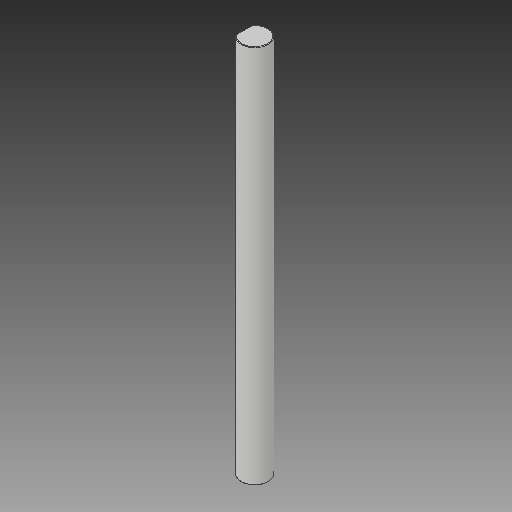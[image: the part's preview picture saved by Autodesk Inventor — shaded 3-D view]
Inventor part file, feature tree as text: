
AUTODESK INVENTOR PART (.ipt)
format: ipt  version: 2019 (Build 230136000, 136)  size: 122,368 bytes
history: native  units: in
note: dims shown in document units (in); Inventor stores cm internally (conversion verified against a paired STEP export)
features: chamfer x1, direct_edit x1, extrude x1, fillet x1, sketch x1, projected_geometry x1, other x1
ambient origin geometry x8: Origin, YZ Plane, XZ Plane, XY Plane, X Axis, Y Axis, Z Axis, Center Point
bodies: Solid1 (feature_tree)
feature tree (7):
  chamfer  "Chamfer1"  Distance=0.505in
  direct_edit  "Direct Edit2"
  extrude  "Extrusion1"  Depth=0.005in
  fillet  "Fillet1"  [1 undecoded]
  sketch  "Sketch1"  dims[d3=-0.005in d4=0.505in d5=0.0in d6=0.005in]
  projected_geometry  "Projected Loop1"
  other  "Size1"
note: 1 required parameter value undecoded (feature->parameter linkage not recoverable at this tier; creation-order binding heuristic only, values carry confidence <= 0.55)
